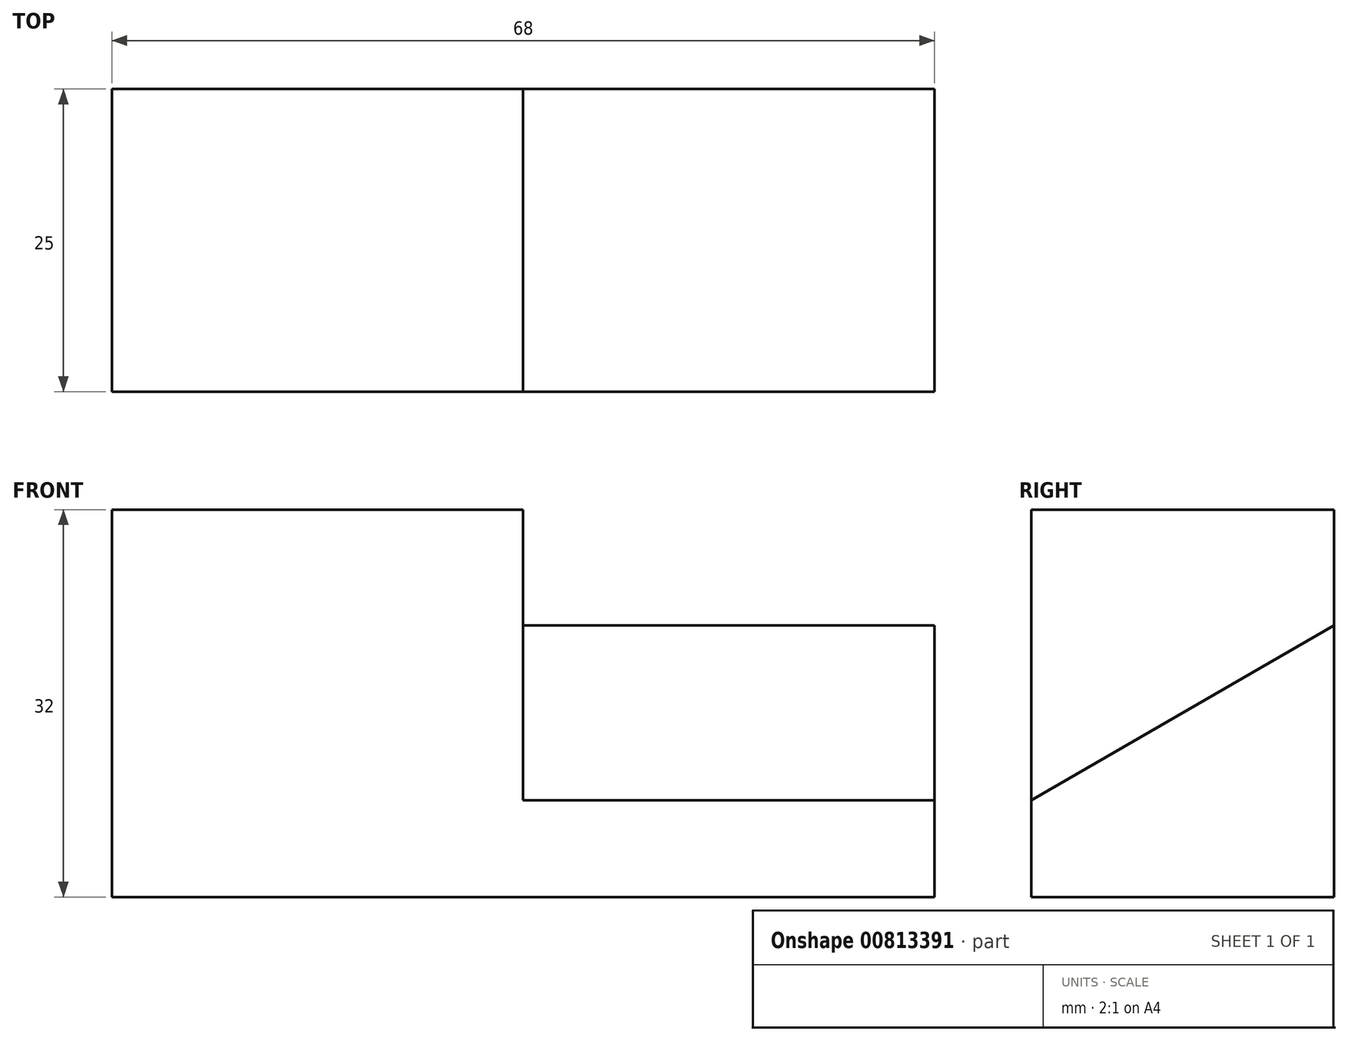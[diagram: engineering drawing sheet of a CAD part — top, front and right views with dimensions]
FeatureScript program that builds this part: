
annotation { "Feature Type Name" : "Feature", "Feature Type Description" : "" }
export const myFeature = defineFeature(function(context is Context, id is Id, definition is map)
    precondition{}
    {
        {
            var Q0;
            Q0=qCreatedBy(makeId("Right.planeOp"),FACE);
            var sketch = newSketch(context, id + "F0", { "sketchPlane" : qUnion([Q0])});
            skLineSegment(sketch, "E0.bottom", {"start": v(0, 0) * mm, "end": v(25, 0) * mm});
            skLineSegment(sketch, "E0.top", {"start": v(0, 32) * mm, "end": v(25, 32) * mm});
            skLineSegment(sketch, "E0.left", {"start": v(0, 0) * mm, "end": v(0, 32) * mm});
            skLineSegment(sketch, "E0.right", {"start": v(25, 0) * mm, "end": v(25, 32) * mm});
            skLineSegment(sketch, "E1", {"start": v(0, 8) * mm, "end": v(25, 22.43) * mm});
            skSolve(sketch);
        }
        {
            var Q0;
            Q0 = qSketchRegion(id + "F0", true);
            extrude(context, id + "F1", {"entities" : qUnion([Q0]), "oppositeDirection" : true, "depth" : 34 * mm, "offsetDistance" : 25 * mm});
        }
        {
            var Q0;
            {var subQ0=sQuery(id+"F0.wireOp",EDGE,"E0.bottom");Q0=makeQuery(id+"F0.imprint","IMPRINT",FACE,{"disambiguationData":[TD([[makeQuery(id+"F0.imprint","IMPRINT",EDGE,{"derivedFrom":subQ0}),1.0]])]});}
            extrude(context, id + "F2", {"entities" : qUnion([Q0]), "operationType" : NewBodyOperationType.ADD, "depth" : (68 - 34) * mm, "offsetDistance" : 25 * mm});
        }
    });
